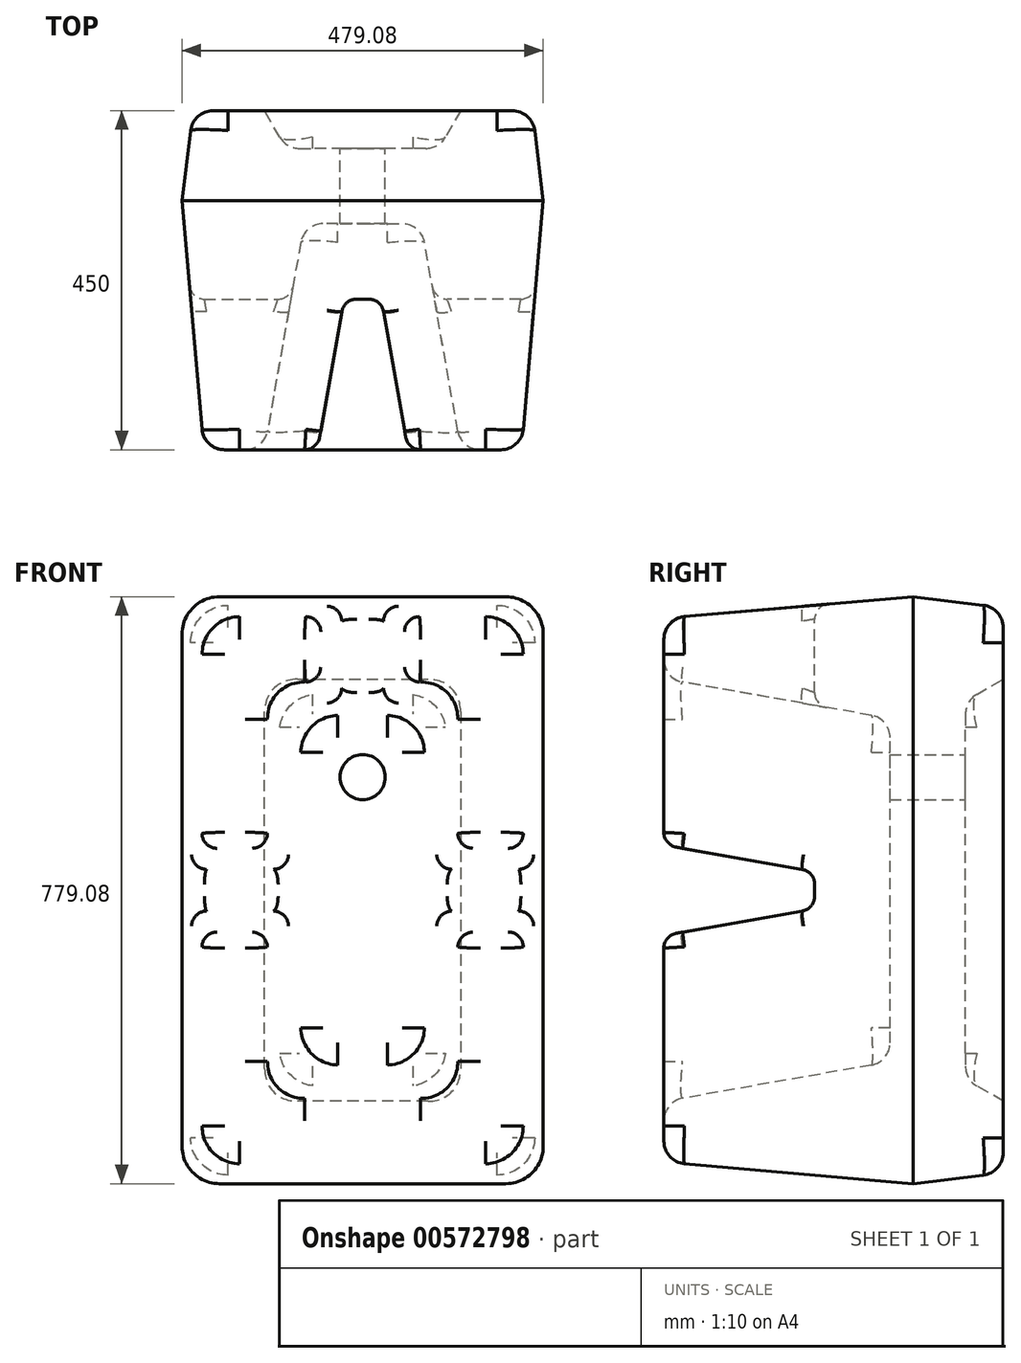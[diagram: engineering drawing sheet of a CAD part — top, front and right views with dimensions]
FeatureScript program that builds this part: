
annotation { "Feature Type Name" : "Feature", "Feature Type Description" : "" }
export const myFeature = defineFeature(function(context is Context, id is Id, definition is map)
    precondition{}
    {
        {
            var Q0;
            Q0=qCreatedBy(makeId("Front.planeOp"),FACE);
            var sketch = newSketch(context, id + "F0", { "sketchPlane" : qUnion([Q0])});
            skLineSegment(sketch, "E0.bottom", {"start": v(0, 0) * mm, "end": v(-500, 0) * mm});
            skLineSegment(sketch, "E0.top", {"start": v(0, 800) * mm, "end": v(-500, 800) * mm});
            skLineSegment(sketch, "E0.left", {"start": v(0, 0) * mm, "end": v(0, 800) * mm});
            skLineSegment(sketch, "E0.right", {"start": v(-500, 0) * mm, "end": v(-500, 800) * mm});
            skSolve(sketch);
        }
        {
            var Q0;
            Q0=makeQuery(id+"F0.imprint","IMPRINT",FACE,{"disambiguationData":[TD([[makeQuery(id+"F0.imprint","IMPRINT",EDGE,{"derivedFrom":sQuery(id+"F0.wireOp",EDGE,"E0.bottom")}),-1.0]])]});
            var sketch = newSketch(context, id + "F1", { "sketchPlane" : qUnion([Q0])});
            skSolve(sketch);
        }
        {
            var Q0;
            Q0=makeQuery(id+"F1.imprint","IMPRINT",FACE,{"disambiguationData":[TD([[makeQuery(id+"F1.imprint","IMPRINT",EDGE,{"derivedFrom":makeQuery(id+"F0.imprint","IMPRINT",EDGE,{"derivedFrom":sQuery(id+"F0.wireOp",EDGE,"E0.bottom")})}),-1.0]])]});
            extrude(context, id + "F2", {"entities" : qUnion([Q0]), "depth" : 450 * mm, "offsetDistance" : 25 * mm, "hasDraft" : true, "draftAngle" : 5 * degree, "draftPullDirection" : true});
        }
        {
            var Q0;
            Q0=makeQuery(id+"F2.opExtrude","CAP_FACE",FACE,{"disambiguationData":[OSD([sQuery(id+"F0.wireOp",EDGE,"E0.bottom"),sQuery(id+"F0.wireOp",EDGE,"E0.top"),sQuery(id+"F0.wireOp",EDGE,"E0.left"),sQuery(id+"F0.wireOp",EDGE,"E0.right")])],"isStart":false});
            var sketch = newSketch(context, id + "F3", { "sketchPlane" : qUnion([Q0])});
            skLineSegment(sketch, "E1.bottom", {"start": v(-380.63, 680.63) * mm, "end": v(-119.37, 680.63) * mm});
            skLineSegment(sketch, "E1.top", {"start": v(-380.63, 119.37) * mm, "end": v(-119.37, 119.37) * mm});
            skLineSegment(sketch, "E1.left", {"start": v(-380.63, 680.63) * mm, "end": v(-380.63, 119.37) * mm});
            skLineSegment(sketch, "E1.right", {"start": v(-119.37, 680.63) * mm, "end": v(-119.37, 119.37) * mm});
            skSolve(sketch);
        }
        {
            var Q0;
            Q0=makeQuery(id+"F3.imprint","IMPRINT",FACE,{"disambiguationData":[TD([[makeQuery(id+"F3.imprint","IMPRINT",EDGE,{"derivedFrom":sQuery(id+"F3.wireOp",EDGE,"E1.bottom")}),-1.0]])]});
            extrude(context, id + "F4", {"entities" : qUnion([Q0]), "operationType" : NewBodyOperationType.REMOVE, "oppositeDirection" : true, "depth" : 300 * mm, "offsetDistance" : 25 * mm, "hasDraft" : true, "draftAngle" : 10 * degree, "draftPullDirection" : true});
        }
        {
            var Q0;
            Q0=makeQuery(id+"F0.imprint","IMPRINT",FACE,{"disambiguationData":[TD([[makeQuery(id+"F0.imprint","IMPRINT",EDGE,{"derivedFrom":sQuery(id+"F0.wireOp",EDGE,"E0.bottom")}),-1.0]])]});
            var sketch = newSketch(context, id + "F5", { "sketchPlane" : qUnion([Q0])});
            skLineSegment(sketch, "E2.bottom", {"start": v(-380, 680) * mm, "end": v(-120, 680) * mm});
            skLineSegment(sketch, "E2.top", {"start": v(-380, 120) * mm, "end": v(-120, 120) * mm});
            skLineSegment(sketch, "E2.left", {"start": v(-380, 680) * mm, "end": v(-380, 120) * mm});
            skLineSegment(sketch, "E2.right", {"start": v(-120, 680) * mm, "end": v(-120, 120) * mm});
            skSolve(sketch);
        }
        {
            var Q0;
            Q0=makeQuery(id+"F5.imprint","IMPRINT",FACE,{"disambiguationData":[TD([[makeQuery(id+"F5.imprint","IMPRINT",EDGE,{"derivedFrom":sQuery(id+"F5.wireOp",EDGE,"E2.bottom")}),-1.0]])]});
            extrude(context, id + "F6", {"entities" : qUnion([Q0]), "operationType" : NewBodyOperationType.REMOVE, "depth" : 50 * mm, "offsetDistance" : 25 * mm, "hasDraft" : true, "draftAngle" : 30 * degree, "draftPullDirection" : true});
        }
        {
            var Q0;
            Q0=makeQuery(id+"F0.imprint","IMPRINT",FACE,{"disambiguationData":[TD([[makeQuery(id+"F0.imprint","IMPRINT",EDGE,{"derivedFrom":sQuery(id+"F0.wireOp",EDGE,"E0.bottom")}),-1.0]])]});
            var sketch = newSketch(context, id + "F7", { "sketchPlane" : qUnion([Q0])});
            skPoint(sketch, "E3", {"position": v(-250, 550) * mm});
            skSolve(sketch);
        }
        {
            var Q0;
            Q0=sQuery(id+"F7.wireOp",VERTEX,"E3");
            var Q1;
            Q1=makeQuery(id+"F2.opExtrude","SWEPT_BODY",BODY,{"disambiguationData":[OSD([sQuery(id+"F0.wireOp",EDGE,"E0.bottom"),sQuery(id+"F0.wireOp",EDGE,"E0.top"),sQuery(id+"F0.wireOp",EDGE,"E0.left"),sQuery(id+"F0.wireOp",EDGE,"E0.right")])]});
            hole(context, id + "F8", {"style" : HoleStyle.SIMPLE, "endStyle" : HoleEndStyle.THROUGH, "oppositeDirection" : true, "holeDiameter" : 60 * mm, "isTappedThrough" : true, "tappedDepth" : 12 * mm, "tapClearance" : 3, "locations" : qUnion([Q0]), "scope" : qUnion([Q1])});
        }
        {
            var Q0;
            Q0=makeQuery(id+"F2.opExtrude","CAP_EDGE",EDGE,{"disambiguationData":[OSD([sQuery(id+"F0.wireOp",EDGE,"E0.left")])],"isStart":true});
            var Q1;
            Q1=makeQuery(id+"F2.opExtrude","CAP_EDGE",EDGE,{"disambiguationData":[OSD([sQuery(id+"F0.wireOp",EDGE,"E0.bottom")])],"isStart":true});
            var Q2;
            Q2=makeQuery(id+"F2.opExtrude","CAP_EDGE",EDGE,{"disambiguationData":[OSD([sQuery(id+"F0.wireOp",EDGE,"E0.right")])],"isStart":true});
            var Q3;
            Q3=makeQuery(id+"F2.opExtrude","CAP_EDGE",EDGE,{"disambiguationData":[OSD([sQuery(id+"F0.wireOp",EDGE,"E0.top")])],"isStart":true});
            chamfer(context, id + "F9", {"entities" : qUnion([Q0, Q1, Q2, Q3]), "chamferType" : ChamferType.TWO_OFFSETS, "width1" : 120 * mm, "oppositeDirection" : false, "width2" : 25 * mm, "tangentPropagation" : true});
        }
        {
            var Q0;
            Q0=makeQuery(id+"F4.boolean.opBoolean","COPY",EDGE,{"derivedFrom":makeQuery(id+"F4.opExtrude","SWEPT_EDGE",EDGE,{"disambiguationData":[OSD([sQuery(id+"F3.wireOp",EDGE,"E1.top"),sQuery(id+"F3.wireOp",EDGE,"E1.right")])]})});
            var Q1;
            Q1=makeQuery(id+"F4.boolean.opBoolean","COPY",EDGE,{"derivedFrom":makeQuery(id+"F4.opExtrude","SWEPT_EDGE",EDGE,{"disambiguationData":[OSD([sQuery(id+"F3.wireOp",EDGE,"E1.bottom"),sQuery(id+"F3.wireOp",EDGE,"E1.right")])]})});
            var Q2;
            Q2=makeQuery(id+"F4.boolean.opBoolean","COPY",EDGE,{"derivedFrom":makeQuery(id+"F4.opExtrude","SWEPT_EDGE",EDGE,{"disambiguationData":[OSD([sQuery(id+"F3.wireOp",EDGE,"E1.bottom"),sQuery(id+"F3.wireOp",EDGE,"E1.left")])]})});
            var Q3;
            Q3=makeQuery(id+"F4.boolean.opBoolean","COPY",EDGE,{"derivedFrom":makeQuery(id+"F4.opExtrude","SWEPT_EDGE",EDGE,{"disambiguationData":[OSD([sQuery(id+"F3.wireOp",EDGE,"E1.top"),sQuery(id+"F3.wireOp",EDGE,"E1.left")])]})});
            var Q4;
            Q4=makeQuery(id+"F2.opExtrude","SWEPT_EDGE",EDGE,{"disambiguationData":[OSD([sQuery(id+"F0.wireOp",EDGE,"E0.bottom"),sQuery(id+"F0.wireOp",EDGE,"E0.left")])]});
            var Q5;
            Q5=makeQuery(id+"F2.opExtrude","SWEPT_EDGE",EDGE,{"disambiguationData":[OSD([sQuery(id+"F0.wireOp",EDGE,"E0.bottom"),sQuery(id+"F0.wireOp",EDGE,"E0.right")])]});
            var Q6;
            Q6=makeQuery(id+"F2.opExtrude","SWEPT_EDGE",EDGE,{"disambiguationData":[OSD([sQuery(id+"F0.wireOp",EDGE,"E0.top"),sQuery(id+"F0.wireOp",EDGE,"E0.left")])]});
            var Q7;
            Q7=makeQuery(id+"F9.opChamfer","BLEND_EDGE",EDGE,{"blendedFrom":[makeQuery(id+"F2.opExtrude","CAP_EDGE",EDGE,{"disambiguationData":[OSD([sQuery(id+"F0.wireOp",EDGE,"E0.bottom")])],"isStart":true}),makeQuery(id+"F2.opExtrude","CAP_EDGE",EDGE,{"disambiguationData":[OSD([sQuery(id+"F0.wireOp",EDGE,"E0.right")])],"isStart":true})],"blendedInto":[]});
            var Q8;
            Q8=makeQuery(id+"F9.opChamfer","BLEND_EDGE",EDGE,{"blendedFrom":[makeQuery(id+"F2.opExtrude","CAP_EDGE",EDGE,{"disambiguationData":[OSD([sQuery(id+"F0.wireOp",EDGE,"E0.bottom")])],"isStart":true}),makeQuery(id+"F2.opExtrude","CAP_EDGE",EDGE,{"disambiguationData":[OSD([sQuery(id+"F0.wireOp",EDGE,"E0.left")])],"isStart":true})],"blendedInto":[]});
            var Q9;
            Q9=makeQuery(id+"F9.opChamfer","BLEND_EDGE",EDGE,{"blendedFrom":[makeQuery(id+"F2.opExtrude","CAP_EDGE",EDGE,{"disambiguationData":[OSD([sQuery(id+"F0.wireOp",EDGE,"E0.top")])],"isStart":true}),makeQuery(id+"F2.opExtrude","CAP_EDGE",EDGE,{"disambiguationData":[OSD([sQuery(id+"F0.wireOp",EDGE,"E0.left")])],"isStart":true})],"blendedInto":[]});
            var Q10;
            Q10=makeQuery(id+"F2.opExtrude","SWEPT_EDGE",EDGE,{"disambiguationData":[OSD([sQuery(id+"F0.wireOp",EDGE,"E0.top"),sQuery(id+"F0.wireOp",EDGE,"E0.right")])]});
            var Q11;
            Q11=makeQuery(id+"F9.opChamfer","BLEND_EDGE",EDGE,{"blendedFrom":[makeQuery(id+"F2.opExtrude","CAP_EDGE",EDGE,{"disambiguationData":[OSD([sQuery(id+"F0.wireOp",EDGE,"E0.top")])],"isStart":true}),makeQuery(id+"F2.opExtrude","CAP_EDGE",EDGE,{"disambiguationData":[OSD([sQuery(id+"F0.wireOp",EDGE,"E0.right")])],"isStart":true})],"blendedInto":[]});
            var Q12;
            Q12=makeQuery(id+"F6.boolean.opBoolean","COPY",EDGE,{"derivedFrom":makeQuery(id+"F6.opExtrude","SWEPT_EDGE",EDGE,{"disambiguationData":[OSD([sQuery(id+"F5.wireOp",EDGE,"E2.bottom"),sQuery(id+"F5.wireOp",EDGE,"E2.right")])]})});
            var Q13;
            Q13=makeQuery(id+"F6.boolean.opBoolean","COPY",EDGE,{"derivedFrom":makeQuery(id+"F6.opExtrude","SWEPT_EDGE",EDGE,{"disambiguationData":[OSD([sQuery(id+"F5.wireOp",EDGE,"E2.bottom"),sQuery(id+"F5.wireOp",EDGE,"E2.left")])]})});
            var Q14;
            Q14=makeQuery(id+"F6.boolean.opBoolean","COPY",EDGE,{"derivedFrom":makeQuery(id+"F6.opExtrude","SWEPT_EDGE",EDGE,{"disambiguationData":[OSD([sQuery(id+"F5.wireOp",EDGE,"E2.top"),sQuery(id+"F5.wireOp",EDGE,"E2.left")])]})});
            var Q15;
            Q15=makeQuery(id+"F6.boolean.opBoolean","COPY",EDGE,{"derivedFrom":makeQuery(id+"F6.opExtrude","SWEPT_EDGE",EDGE,{"disambiguationData":[OSD([sQuery(id+"F5.wireOp",EDGE,"E2.top"),sQuery(id+"F5.wireOp",EDGE,"E2.right")])]})});
            fillet(context, id + "F10", {"entities" : qUnion([Q0, Q1, Q2, Q3, Q4, Q5, Q6, Q7, Q8, Q9, Q10, Q11, Q12, Q13, Q14, Q15]), "radius" : 50 * mm, "tangentPropagation" : true, "defaultsChanged" : true, "vertexSettings" : [], "allowEdgeOverflow" : false});
        }
        {
            var Q0;
            {var subQ0=sQuery(id+"F3.wireOp",EDGE,"E1.right");var subQ1=sQuery(id+"F3.wireOp",EDGE,"E1.bottom");Q0=makeQuery(id+"F10.opFillet","BLEND_EDGE",EDGE,{"blendedFrom":[makeQuery(id+"F4.boolean.opBoolean","COPY",EDGE,{"derivedFrom":makeQuery(id+"F4.opExtrude","SWEPT_EDGE",EDGE,{"disambiguationData":[OSD([subQ1,subQ0])]})}),makeQuery(id+"F4.boolean.opBoolean","COPY",FACE,{"derivedFrom":makeQuery(id+"F4.opExtrude","CAP_FACE",FACE,{"disambiguationData":[OSD([subQ1,sQuery(id+"F3.wireOp",EDGE,"E1.top"),sQuery(id+"F3.wireOp",EDGE,"E1.left"),subQ0])],"isStart":false})})],"blendedInto":[makeQuery(id+"F4.boolean.opBoolean","COPY",FACE,{"derivedFrom":makeQuery(id+"F4.opExtrude","CAP_FACE",FACE,{"disambiguationData":[OSD([subQ1,sQuery(id+"F3.wireOp",EDGE,"E1.top"),sQuery(id+"F3.wireOp",EDGE,"E1.left"),subQ0])],"isStart":false})})]});}
            var Q1;
            Q1=makeQuery(id+"F10.opFillet","BLEND_EDGE",EDGE,{"blendedFrom":[makeQuery(id+"F4.boolean.opBoolean","COPY",EDGE,{"derivedFrom":makeQuery(id+"F4.opExtrude","SWEPT_EDGE",EDGE,{"disambiguationData":[OSD([sQuery(id+"F3.wireOp",EDGE,"E1.bottom"),sQuery(id+"F3.wireOp",EDGE,"E1.right")])]})}),makeQuery(id+"F2.opExtrude","CAP_FACE",FACE,{"disambiguationData":[OSD([sQuery(id+"F0.wireOp",EDGE,"E0.bottom"),sQuery(id+"F0.wireOp",EDGE,"E0.top"),sQuery(id+"F0.wireOp",EDGE,"E0.left"),sQuery(id+"F0.wireOp",EDGE,"E0.right")])],"isStart":false})],"blendedInto":[makeQuery(id+"F2.opExtrude","CAP_FACE",FACE,{"disambiguationData":[OSD([sQuery(id+"F0.wireOp",EDGE,"E0.bottom"),sQuery(id+"F0.wireOp",EDGE,"E0.top"),sQuery(id+"F0.wireOp",EDGE,"E0.left"),sQuery(id+"F0.wireOp",EDGE,"E0.right")])],"isStart":false})]});
            var Q2;
            {var subQ0=sQuery(id+"F0.wireOp",EDGE,"E0.left");var subQ1=sQuery(id+"F0.wireOp",EDGE,"E0.top");Q2=makeQuery(id+"F10.opFillet","BLEND_EDGE",EDGE,{"blendedFrom":[makeQuery(id+"F2.opExtrude","SWEPT_EDGE",EDGE,{"disambiguationData":[OSD([subQ1,subQ0])]}),makeQuery(id+"F2.opExtrude","CAP_FACE",FACE,{"disambiguationData":[OSD([sQuery(id+"F0.wireOp",EDGE,"E0.bottom"),subQ1,subQ0,sQuery(id+"F0.wireOp",EDGE,"E0.right")])],"isStart":false})],"blendedInto":[makeQuery(id+"F2.opExtrude","CAP_FACE",FACE,{"disambiguationData":[OSD([sQuery(id+"F0.wireOp",EDGE,"E0.bottom"),subQ1,subQ0,sQuery(id+"F0.wireOp",EDGE,"E0.right")])],"isStart":false})]});}
            var Q3;
            {var subQ0=sQuery(id+"F0.wireOp",EDGE,"E0.left");Q3=makeQuery(id+"F9.opChamfer","BLEND_EDGE",EDGE,{"blendedFrom":[makeQuery(id+"F2.opExtrude","CAP_EDGE",EDGE,{"disambiguationData":[OSD([subQ0])],"isStart":true}),makeQuery(id+"F2.opExtrude","CAP_FACE",FACE,{"disambiguationData":[OSD([sQuery(id+"F0.wireOp",EDGE,"E0.bottom"),sQuery(id+"F0.wireOp",EDGE,"E0.top"),subQ0,sQuery(id+"F0.wireOp",EDGE,"E0.right")])],"isStart":true})],"blendedInto":[makeQuery(id+"F2.opExtrude","CAP_FACE",FACE,{"disambiguationData":[OSD([sQuery(id+"F0.wireOp",EDGE,"E0.bottom"),sQuery(id+"F0.wireOp",EDGE,"E0.top"),subQ0,sQuery(id+"F0.wireOp",EDGE,"E0.right")])],"isStart":true})]});}
            var Q4;
            Q4=makeQuery(id+"F6.boolean.opBoolean","COPY",EDGE,{"derivedFrom":makeQuery(id+"F6.opExtrude","CAP_EDGE",EDGE,{"disambiguationData":[OSD([sQuery(id+"F5.wireOp",EDGE,"E2.top")])],"isStart":true})});
            var Q5;
            Q5=makeQuery(id+"F6.boolean.opBoolean","COPY",EDGE,{"derivedFrom":makeQuery(id+"F6.opExtrude","CAP_EDGE",EDGE,{"disambiguationData":[OSD([sQuery(id+"F5.wireOp",EDGE,"E2.top")])],"isStart":false})});
            fillet(context, id + "F11", {"entities" : qUnion([Q0, Q1, Q2, Q3, Q4, Q5]), "radius" : 30 * mm, "tangentPropagation" : true, "allowEdgeOverflow" : false});
        }
        {
            var Q0;
            Q0=makeQuery(id+"F2.opExtrude","CAP_FACE",FACE,{"disambiguationData":[OSD([sQuery(id+"F0.wireOp",EDGE,"E0.bottom"),sQuery(id+"F0.wireOp",EDGE,"E0.top"),sQuery(id+"F0.wireOp",EDGE,"E0.left"),sQuery(id+"F0.wireOp",EDGE,"E0.right")])],"isStart":false});
            var sketch = newSketch(context, id + "F12", { "sketchPlane" : qUnion([Q0])});
            skLineSegment(sketch, "E4.bottom", {"start": v(-190, 257.75) * mm, "end": v(-310, 257.75) * mm});
            skLineSegment(sketch, "E4.top", {"start": v(-190, 1153.86) * mm, "end": v(-310, 1153.86) * mm});
            skLineSegment(sketch, "E4.left", {"start": v(-190, 257.75) * mm, "end": v(-190, 1153.86) * mm});
            skLineSegment(sketch, "E4.right", {"start": v(-310, 257.75) * mm, "end": v(-310, 1153.86) * mm});
            skPoint(sketch, "E4.middle", {"position": v(-250, 705.8) * mm});
            skLineSegment(sketch, "E5.bottom", {"start": v(130.25, 340) * mm, "end": v(-941.86, 340) * mm});
            skLineSegment(sketch, "E5.top", {"start": v(130.25, 460) * mm, "end": v(-941.86, 460) * mm});
            skLineSegment(sketch, "E5.left", {"start": v(130.25, 340) * mm, "end": v(130.25, 460) * mm});
            skLineSegment(sketch, "E5.right", {"start": v(-941.86, 340) * mm, "end": v(-941.86, 460) * mm});
            skPoint(sketch, "E5.middle", {"position": v(-405.8, 400) * mm});
            skSolve(sketch);
        }
        {
            var Q0;
            {var subQ0=sQuery(id+"F12.wireOp",EDGE,"E5.bottom");var subQ1=sQuery(id+"F12.wireOp",EDGE,"E4.right");var subQ2=makeQuery(id+"F12.imprint","INTERSECT",VERTEX,{"derivedFrom":[subQ1,subQ0]});Q0=makeQuery(id+"F12.imprint","IMPRINT",FACE,{"disambiguationData":[TD([[makeQuery(id+"F12.imprint","IMPRINT",EDGE,{"disambiguationData":[TD([[subQ2,-1.0]])],"derivedFrom":subQ1}),1.0]])]});}
            var Q1;
            {var subQ0=sQuery(id+"F12.wireOp",EDGE,"E5.bottom");var subQ1=sQuery(id+"F0.wireOp",EDGE,"E0.right");var subQ2=makeQuery(id+"F2.opExtrude","CAP_FACE",FACE,{"disambiguationData":[OSD([sQuery(id+"F0.wireOp",EDGE,"E0.bottom"),sQuery(id+"F0.wireOp",EDGE,"E0.top"),sQuery(id+"F0.wireOp",EDGE,"E0.left"),subQ1])],"isStart":false});var subQ3=makeQuery(id+"F11.opFillet","BLEND_EDGE",EDGE,{"blendedFrom":[makeQuery(id+"F2.opExtrude","CAP_EDGE",EDGE,{"disambiguationData":[OSD([subQ1])],"isStart":false}),subQ2],"blendedInto":[subQ2]});var subQ4=makeQuery(id+"F12.imprint","INTERSECT",VERTEX,{"derivedFrom":[subQ3,subQ0]});Q1=makeQuery(id+"F12.imprint","IMPRINT",FACE,{"disambiguationData":[TD([[makeQuery(id+"F12.imprint","IMPRINT",EDGE,{"disambiguationData":[TD([[subQ4,1.0]])],"derivedFrom":subQ0}),-1.0]])]});}
            var Q2;
            {var subQ0=sQuery(id+"F12.wireOp",EDGE,"E5.right");Q2=makeQuery(id+"F12.imprint","IMPRINT",FACE,{"disambiguationData":[TD([[makeQuery(id+"F12.imprint","IMPRINT",EDGE,{"derivedFrom":subQ0}),-1.0]])]});}
            var Q3;
            {var subQ0=sQuery(id+"F12.wireOp",EDGE,"E5.bottom");var subQ1=sQuery(id+"F12.wireOp",EDGE,"E4.left");var subQ2=makeQuery(id+"F12.imprint","INTERSECT",VERTEX,{"derivedFrom":[subQ1,subQ0]});Q3=makeQuery(id+"F12.imprint","IMPRINT",FACE,{"disambiguationData":[TD([[makeQuery(id+"F12.imprint","IMPRINT",EDGE,{"disambiguationData":[TD([[subQ2,-1.0]])],"derivedFrom":subQ1}),1.0]])]});}
            var Q4;
            {var subQ0=sQuery(id+"F12.wireOp",EDGE,"E5.top");var subQ1=sQuery(id+"F12.wireOp",EDGE,"E4.left");var subQ2=makeQuery(id+"F12.imprint","INTERSECT",VERTEX,{"derivedFrom":[subQ1,subQ0]});Q4=makeQuery(id+"F12.imprint","IMPRINT",FACE,{"disambiguationData":[TD([[makeQuery(id+"F12.imprint","IMPRINT",EDGE,{"disambiguationData":[TD([[subQ2,-1.0]])],"derivedFrom":subQ0}),-1.0]])]});}
            var Q5;
            {var subQ0=sQuery(id+"F12.wireOp",EDGE,"E5.bottom");var subQ1=sQuery(id+"F12.wireOp",EDGE,"E4.left");var subQ2=makeQuery(id+"F12.imprint","INTERSECT",VERTEX,{"derivedFrom":[subQ1,subQ0]});Q5=makeQuery(id+"F12.imprint","IMPRINT",FACE,{"disambiguationData":[TD([[makeQuery(id+"F12.imprint","IMPRINT",EDGE,{"disambiguationData":[TD([[subQ2,-1.0]])],"derivedFrom":subQ0}),1.0]])]});}
            var Q6;
            {var subQ0=sQuery(id+"F12.wireOp",EDGE,"E5.bottom");var subQ1=sQuery(id+"F12.wireOp",EDGE,"E4.left");var subQ2=makeQuery(id+"F12.imprint","INTERSECT",VERTEX,{"derivedFrom":[subQ1,subQ0]});Q6=makeQuery(id+"F12.imprint","IMPRINT",FACE,{"disambiguationData":[TD([[makeQuery(id+"F12.imprint","IMPRINT",EDGE,{"disambiguationData":[TD([[subQ2,-1.0]])],"derivedFrom":subQ1}),-1.0]])]});}
            var Q7;
            {var subQ0=sQuery(id+"F12.wireOp",EDGE,"E5.bottom");var subQ1=sQuery(id+"F0.wireOp",EDGE,"E0.left");var subQ2=makeQuery(id+"F2.opExtrude","CAP_FACE",FACE,{"disambiguationData":[OSD([sQuery(id+"F0.wireOp",EDGE,"E0.bottom"),sQuery(id+"F0.wireOp",EDGE,"E0.top"),subQ1,sQuery(id+"F0.wireOp",EDGE,"E0.right")])],"isStart":false});var subQ3=makeQuery(id+"F11.opFillet","BLEND_EDGE",EDGE,{"blendedFrom":[makeQuery(id+"F2.opExtrude","CAP_EDGE",EDGE,{"disambiguationData":[OSD([subQ1])],"isStart":false}),subQ2],"blendedInto":[subQ2]});var subQ4=makeQuery(id+"F12.imprint","INTERSECT",VERTEX,{"derivedFrom":[subQ3,subQ0]});Q7=makeQuery(id+"F12.imprint","IMPRINT",FACE,{"disambiguationData":[TD([[makeQuery(id+"F12.imprint","IMPRINT",EDGE,{"disambiguationData":[TD([[subQ4,-1.0]])],"derivedFrom":subQ0}),-1.0]])]});}
            var Q8;
            {var subQ0=sQuery(id+"F12.wireOp",EDGE,"E5.left");Q8=makeQuery(id+"F12.imprint","IMPRINT",FACE,{"disambiguationData":[TD([[makeQuery(id+"F12.imprint","IMPRINT",EDGE,{"derivedFrom":subQ0}),1.0]])]});}
            var Q9;
            {var subQ0=sQuery(id+"F12.wireOp",EDGE,"E4.bottom");Q9=makeQuery(id+"F12.imprint","IMPRINT",FACE,{"disambiguationData":[TD([[makeQuery(id+"F12.imprint","IMPRINT",EDGE,{"derivedFrom":subQ0}),-1.0]])]});}
            var Q10;
            {var subQ0=sQuery(id+"F12.wireOp",EDGE,"E4.left");var subQ1=sQuery(id+"F0.wireOp",EDGE,"E0.bottom");var subQ2=makeQuery(id+"F2.opExtrude","CAP_FACE",FACE,{"disambiguationData":[OSD([subQ1,sQuery(id+"F0.wireOp",EDGE,"E0.top"),sQuery(id+"F0.wireOp",EDGE,"E0.left"),sQuery(id+"F0.wireOp",EDGE,"E0.right")])],"isStart":false});var subQ3=makeQuery(id+"F11.opFillet","BLEND_EDGE",EDGE,{"blendedFrom":[makeQuery(id+"F2.opExtrude","CAP_EDGE",EDGE,{"disambiguationData":[OSD([subQ1])],"isStart":false}),subQ2],"blendedInto":[subQ2]});var subQ4=makeQuery(id+"F12.imprint","INTERSECT",VERTEX,{"derivedFrom":[subQ3,subQ0]});Q10=makeQuery(id+"F12.imprint","IMPRINT",FACE,{"disambiguationData":[TD([[makeQuery(id+"F12.imprint","IMPRINT",EDGE,{"disambiguationData":[TD([[subQ4,-1.0]])],"derivedFrom":subQ0}),1.0]])]});}
            var Q11;
            {var subQ0=sQuery(id+"F12.wireOp",EDGE,"E4.left");var subQ1=sQuery(id+"F0.wireOp",EDGE,"E0.top");var subQ2=makeQuery(id+"F2.opExtrude","CAP_FACE",FACE,{"disambiguationData":[OSD([sQuery(id+"F0.wireOp",EDGE,"E0.bottom"),subQ1,sQuery(id+"F0.wireOp",EDGE,"E0.left"),sQuery(id+"F0.wireOp",EDGE,"E0.right")])],"isStart":false});var subQ3=makeQuery(id+"F11.opFillet","BLEND_EDGE",EDGE,{"blendedFrom":[makeQuery(id+"F2.opExtrude","CAP_EDGE",EDGE,{"disambiguationData":[OSD([subQ1])],"isStart":false}),subQ2],"blendedInto":[subQ2]});var subQ4=makeQuery(id+"F12.imprint","INTERSECT",VERTEX,{"derivedFrom":[subQ3,subQ0]});Q11=makeQuery(id+"F12.imprint","IMPRINT",FACE,{"disambiguationData":[TD([[makeQuery(id+"F12.imprint","IMPRINT",EDGE,{"disambiguationData":[TD([[subQ4,1.0]])],"derivedFrom":subQ0}),1.0]])]});}
            var Q12;
            {var subQ0=sQuery(id+"F12.wireOp",EDGE,"E4.top");Q12=makeQuery(id+"F12.imprint","IMPRINT",FACE,{"disambiguationData":[TD([[makeQuery(id+"F12.imprint","IMPRINT",EDGE,{"derivedFrom":subQ0}),1.0]])]});}
            extrude(context, id + "F13", {"entities" : qUnion([Q0, Q1, Q2, Q3, Q4, Q5, Q6, Q7, Q8, Q9, Q10, Q11, Q12]), "operationType" : NewBodyOperationType.REMOVE, "oppositeDirection" : true, "depth" : 200 * mm, "offsetDistance" : 25 * mm, "hasDraft" : true, "draftAngle" : 10 * degree, "draftPullDirection" : true});
        }
        {
            var Q0;
            {var subQ0=sQuery(id+"F12.wireOp",EDGE,"E5.top");var subQ1=sQuery(id+"F0.wireOp",EDGE,"E0.right");var subQ2=makeQuery(id+"F2.opExtrude","CAP_FACE",FACE,{"disambiguationData":[OSD([sQuery(id+"F0.wireOp",EDGE,"E0.bottom"),sQuery(id+"F0.wireOp",EDGE,"E0.top"),sQuery(id+"F0.wireOp",EDGE,"E0.left"),subQ1])],"isStart":false});var subQ3=makeQuery(id+"F12.imprint","INTERSECT",VERTEX,{"derivedFrom":[makeQuery(id+"F11.opFillet","BLEND_EDGE",EDGE,{"blendedFrom":[makeQuery(id+"F2.opExtrude","CAP_EDGE",EDGE,{"disambiguationData":[OSD([subQ1])],"isStart":false}),subQ2],"blendedInto":[subQ2]}),subQ0]});Q0=makeQuery(id+"F13.boolean.opBoolean","COPY",EDGE,{"derivedFrom":makeQuery(id+"F13.opExtrude","CAP_EDGE",EDGE,{"disambiguationData":[OSD([subQ0]),TDD([makeQuery(id+"F12.imprint","IMPRINT",EDGE,{"disambiguationData":[TD([[makeQuery(id+"F12.imprint","INTERSECT",VERTEX,{"derivedFrom":[sQuery(id+"F12.wireOp",EDGE,"E4.right"),subQ0]}),-1.0]])],"derivedFrom":subQ0}),makeQuery(id+"F12.imprint","IMPRINT",EDGE,{"disambiguationData":[TD([[subQ3,1.0]])],"derivedFrom":subQ0}),makeQuery(id+"F12.imprint","IMPRINT",EDGE,{"disambiguationData":[TD([[makeQuery(id+"F12.imprint","INTERSECT",VERTEX,{"derivedFrom":[subQ0,sQuery(id+"F12.wireOp",EDGE,"E5.right")]}),1.0]])],"derivedFrom":subQ0})])],"isStart":false})});}
            var Q1;
            {var subQ0=sQuery(id+"F12.wireOp",EDGE,"E5.bottom");var subQ1=sQuery(id+"F0.wireOp",EDGE,"E0.right");var subQ2=makeQuery(id+"F2.opExtrude","CAP_FACE",FACE,{"disambiguationData":[OSD([sQuery(id+"F0.wireOp",EDGE,"E0.bottom"),sQuery(id+"F0.wireOp",EDGE,"E0.top"),sQuery(id+"F0.wireOp",EDGE,"E0.left"),subQ1])],"isStart":false});var subQ3=makeQuery(id+"F12.imprint","INTERSECT",VERTEX,{"derivedFrom":[makeQuery(id+"F11.opFillet","BLEND_EDGE",EDGE,{"blendedFrom":[makeQuery(id+"F2.opExtrude","CAP_EDGE",EDGE,{"disambiguationData":[OSD([subQ1])],"isStart":false}),subQ2],"blendedInto":[subQ2]}),subQ0]});Q1=makeQuery(id+"F13.boolean.opBoolean","COPY",EDGE,{"derivedFrom":makeQuery(id+"F13.opExtrude","CAP_EDGE",EDGE,{"disambiguationData":[OSD([subQ0]),TDD([makeQuery(id+"F12.imprint","IMPRINT",EDGE,{"disambiguationData":[TD([[makeQuery(id+"F12.imprint","INTERSECT",VERTEX,{"derivedFrom":[sQuery(id+"F12.wireOp",EDGE,"E4.right"),subQ0]}),-1.0]])],"derivedFrom":subQ0}),makeQuery(id+"F12.imprint","IMPRINT",EDGE,{"disambiguationData":[TD([[subQ3,1.0]])],"derivedFrom":subQ0}),makeQuery(id+"F12.imprint","IMPRINT",EDGE,{"disambiguationData":[TD([[makeQuery(id+"F12.imprint","INTERSECT",VERTEX,{"derivedFrom":[subQ0,sQuery(id+"F12.wireOp",EDGE,"E5.right")]}),1.0]])],"derivedFrom":subQ0})])],"isStart":false})});}
            var Q2;
            {var subQ0=sQuery(id+"F12.wireOp",EDGE,"E4.right");var subQ1=sQuery(id+"F0.wireOp",EDGE,"E0.top");var subQ2=makeQuery(id+"F2.opExtrude","CAP_FACE",FACE,{"disambiguationData":[OSD([sQuery(id+"F0.wireOp",EDGE,"E0.bottom"),subQ1,sQuery(id+"F0.wireOp",EDGE,"E0.left"),sQuery(id+"F0.wireOp",EDGE,"E0.right")])],"isStart":false});var subQ3=makeQuery(id+"F12.imprint","INTERSECT",VERTEX,{"derivedFrom":[makeQuery(id+"F11.opFillet","BLEND_EDGE",EDGE,{"blendedFrom":[makeQuery(id+"F2.opExtrude","CAP_EDGE",EDGE,{"disambiguationData":[OSD([subQ1])],"isStart":false}),subQ2],"blendedInto":[subQ2]}),subQ0]});Q2=makeQuery(id+"F13.boolean.opBoolean","COPY",EDGE,{"derivedFrom":makeQuery(id+"F13.opExtrude","CAP_EDGE",EDGE,{"disambiguationData":[OSD([subQ0]),TDD([makeQuery(id+"F12.imprint","IMPRINT",EDGE,{"disambiguationData":[TD([[makeQuery(id+"F12.imprint","INTERSECT",VERTEX,{"derivedFrom":[subQ0,sQuery(id+"F12.wireOp",EDGE,"E5.top")]}),-1.0]])],"derivedFrom":subQ0}),makeQuery(id+"F12.imprint","IMPRINT",EDGE,{"disambiguationData":[TD([[subQ3,1.0]])],"derivedFrom":subQ0}),makeQuery(id+"F12.imprint","IMPRINT",EDGE,{"disambiguationData":[TD([[makeQuery(id+"F12.imprint","INTERSECT",VERTEX,{"derivedFrom":[sQuery(id+"F12.wireOp",EDGE,"E4.top"),subQ0]}),1.0]])],"derivedFrom":subQ0})])],"isStart":false})});}
            var Q3;
            {var subQ0=sQuery(id+"F12.wireOp",EDGE,"E4.left");var subQ1=sQuery(id+"F0.wireOp",EDGE,"E0.top");var subQ2=makeQuery(id+"F2.opExtrude","CAP_FACE",FACE,{"disambiguationData":[OSD([sQuery(id+"F0.wireOp",EDGE,"E0.bottom"),subQ1,sQuery(id+"F0.wireOp",EDGE,"E0.left"),sQuery(id+"F0.wireOp",EDGE,"E0.right")])],"isStart":false});var subQ3=makeQuery(id+"F12.imprint","INTERSECT",VERTEX,{"derivedFrom":[makeQuery(id+"F11.opFillet","BLEND_EDGE",EDGE,{"blendedFrom":[makeQuery(id+"F2.opExtrude","CAP_EDGE",EDGE,{"disambiguationData":[OSD([subQ1])],"isStart":false}),subQ2],"blendedInto":[subQ2]}),subQ0]});Q3=makeQuery(id+"F13.boolean.opBoolean","COPY",EDGE,{"derivedFrom":makeQuery(id+"F13.opExtrude","CAP_EDGE",EDGE,{"disambiguationData":[OSD([subQ0]),TDD([makeQuery(id+"F12.imprint","IMPRINT",EDGE,{"disambiguationData":[TD([[makeQuery(id+"F12.imprint","INTERSECT",VERTEX,{"derivedFrom":[subQ0,sQuery(id+"F12.wireOp",EDGE,"E5.top")]}),-1.0]])],"derivedFrom":subQ0}),makeQuery(id+"F12.imprint","IMPRINT",EDGE,{"disambiguationData":[TD([[subQ3,1.0]])],"derivedFrom":subQ0}),makeQuery(id+"F12.imprint","IMPRINT",EDGE,{"disambiguationData":[TD([[makeQuery(id+"F12.imprint","INTERSECT",VERTEX,{"derivedFrom":[sQuery(id+"F12.wireOp",EDGE,"E4.top"),subQ0]}),1.0]])],"derivedFrom":subQ0})])],"isStart":false})});}
            var Q4;
            {var subQ0=sQuery(id+"F12.wireOp",EDGE,"E5.bottom");var subQ1=sQuery(id+"F0.wireOp",EDGE,"E0.left");var subQ2=makeQuery(id+"F2.opExtrude","CAP_FACE",FACE,{"disambiguationData":[OSD([sQuery(id+"F0.wireOp",EDGE,"E0.bottom"),sQuery(id+"F0.wireOp",EDGE,"E0.top"),subQ1,sQuery(id+"F0.wireOp",EDGE,"E0.right")])],"isStart":false});var subQ4=makeQuery(id+"F12.imprint","INTERSECT",VERTEX,{"derivedFrom":[makeQuery(id+"F11.opFillet","BLEND_EDGE",EDGE,{"blendedFrom":[makeQuery(id+"F2.opExtrude","CAP_EDGE",EDGE,{"disambiguationData":[OSD([subQ1])],"isStart":false}),subQ2],"blendedInto":[subQ2]}),subQ0]});Q4=makeQuery(id+"F13.boolean.opBoolean","COPY",EDGE,{"derivedFrom":makeQuery(id+"F13.opExtrude","CAP_EDGE",EDGE,{"disambiguationData":[OSD([subQ0]),TDD([makeQuery(id+"F12.imprint","IMPRINT",EDGE,{"disambiguationData":[TD([[makeQuery(id+"F12.imprint","INTERSECT",VERTEX,{"derivedFrom":[subQ0,sQuery(id+"F12.wireOp",EDGE,"E5.left")]}),-1.0]])],"derivedFrom":subQ0}),makeQuery(id+"F12.imprint","IMPRINT",EDGE,{"disambiguationData":[TD([[subQ4,-1.0]])],"derivedFrom":subQ0}),makeQuery(id+"F12.imprint","IMPRINT",EDGE,{"disambiguationData":[TD([[makeQuery(id+"F12.imprint","INTERSECT",VERTEX,{"derivedFrom":[sQuery(id+"F12.wireOp",EDGE,"E4.left"),subQ0]}),1.0]])],"derivedFrom":subQ0})])],"isStart":false})});}
            var Q5;
            {var subQ0=sQuery(id+"F12.wireOp",EDGE,"E5.top");var subQ1=sQuery(id+"F0.wireOp",EDGE,"E0.left");var subQ2=makeQuery(id+"F2.opExtrude","CAP_FACE",FACE,{"disambiguationData":[OSD([sQuery(id+"F0.wireOp",EDGE,"E0.bottom"),sQuery(id+"F0.wireOp",EDGE,"E0.top"),subQ1,sQuery(id+"F0.wireOp",EDGE,"E0.right")])],"isStart":false});var subQ4=makeQuery(id+"F12.imprint","INTERSECT",VERTEX,{"derivedFrom":[makeQuery(id+"F11.opFillet","BLEND_EDGE",EDGE,{"blendedFrom":[makeQuery(id+"F2.opExtrude","CAP_EDGE",EDGE,{"disambiguationData":[OSD([subQ1])],"isStart":false}),subQ2],"blendedInto":[subQ2]}),subQ0]});Q5=makeQuery(id+"F13.boolean.opBoolean","COPY",EDGE,{"derivedFrom":makeQuery(id+"F13.opExtrude","CAP_EDGE",EDGE,{"disambiguationData":[OSD([subQ0]),TDD([makeQuery(id+"F12.imprint","IMPRINT",EDGE,{"disambiguationData":[TD([[makeQuery(id+"F12.imprint","INTERSECT",VERTEX,{"derivedFrom":[subQ0,sQuery(id+"F12.wireOp",EDGE,"E5.left")]}),-1.0]])],"derivedFrom":subQ0}),makeQuery(id+"F12.imprint","IMPRINT",EDGE,{"disambiguationData":[TD([[subQ4,-1.0]])],"derivedFrom":subQ0}),makeQuery(id+"F12.imprint","IMPRINT",EDGE,{"disambiguationData":[TD([[makeQuery(id+"F12.imprint","INTERSECT",VERTEX,{"derivedFrom":[sQuery(id+"F12.wireOp",EDGE,"E4.left"),subQ0]}),1.0]])],"derivedFrom":subQ0})])],"isStart":false})});}
            var Q6;
            {var subQ0=sQuery(id+"F12.wireOp",EDGE,"E4.right");var subQ1=sQuery(id+"F0.wireOp",EDGE,"E0.bottom");var subQ2=makeQuery(id+"F2.opExtrude","CAP_FACE",FACE,{"disambiguationData":[OSD([subQ1,sQuery(id+"F0.wireOp",EDGE,"E0.top"),sQuery(id+"F0.wireOp",EDGE,"E0.left"),sQuery(id+"F0.wireOp",EDGE,"E0.right")])],"isStart":false});var subQ4=makeQuery(id+"F12.imprint","INTERSECT",VERTEX,{"derivedFrom":[makeQuery(id+"F11.opFillet","BLEND_EDGE",EDGE,{"blendedFrom":[makeQuery(id+"F2.opExtrude","CAP_EDGE",EDGE,{"disambiguationData":[OSD([subQ1])],"isStart":false}),subQ2],"blendedInto":[subQ2]}),subQ0]});Q6=makeQuery(id+"F13.boolean.opBoolean","COPY",EDGE,{"derivedFrom":makeQuery(id+"F13.opExtrude","CAP_EDGE",EDGE,{"disambiguationData":[OSD([subQ0]),TDD([makeQuery(id+"F12.imprint","IMPRINT",EDGE,{"disambiguationData":[TD([[makeQuery(id+"F12.imprint","INTERSECT",VERTEX,{"derivedFrom":[sQuery(id+"F12.wireOp",EDGE,"E4.bottom"),subQ0]}),-1.0]])],"derivedFrom":subQ0}),makeQuery(id+"F12.imprint","IMPRINT",EDGE,{"disambiguationData":[TD([[subQ4,-1.0]])],"derivedFrom":subQ0}),makeQuery(id+"F12.imprint","IMPRINT",EDGE,{"disambiguationData":[TD([[makeQuery(id+"F12.imprint","INTERSECT",VERTEX,{"derivedFrom":[subQ0,sQuery(id+"F12.wireOp",EDGE,"E5.bottom")]}),1.0]])],"derivedFrom":subQ0})])],"isStart":false})});}
            var Q7;
            {var subQ0=sQuery(id+"F12.wireOp",EDGE,"E4.left");var subQ1=sQuery(id+"F0.wireOp",EDGE,"E0.bottom");var subQ2=makeQuery(id+"F2.opExtrude","CAP_FACE",FACE,{"disambiguationData":[OSD([subQ1,sQuery(id+"F0.wireOp",EDGE,"E0.top"),sQuery(id+"F0.wireOp",EDGE,"E0.left"),sQuery(id+"F0.wireOp",EDGE,"E0.right")])],"isStart":false});var subQ4=makeQuery(id+"F12.imprint","INTERSECT",VERTEX,{"derivedFrom":[makeQuery(id+"F11.opFillet","BLEND_EDGE",EDGE,{"blendedFrom":[makeQuery(id+"F2.opExtrude","CAP_EDGE",EDGE,{"disambiguationData":[OSD([subQ1])],"isStart":false}),subQ2],"blendedInto":[subQ2]}),subQ0]});Q7=makeQuery(id+"F13.boolean.opBoolean","COPY",EDGE,{"derivedFrom":makeQuery(id+"F13.opExtrude","CAP_EDGE",EDGE,{"disambiguationData":[OSD([subQ0]),TDD([makeQuery(id+"F12.imprint","IMPRINT",EDGE,{"disambiguationData":[TD([[makeQuery(id+"F12.imprint","INTERSECT",VERTEX,{"derivedFrom":[sQuery(id+"F12.wireOp",EDGE,"E4.bottom"),subQ0]}),-1.0]])],"derivedFrom":subQ0}),makeQuery(id+"F12.imprint","IMPRINT",EDGE,{"disambiguationData":[TD([[subQ4,-1.0]])],"derivedFrom":subQ0}),makeQuery(id+"F12.imprint","IMPRINT",EDGE,{"disambiguationData":[TD([[makeQuery(id+"F12.imprint","INTERSECT",VERTEX,{"derivedFrom":[subQ0,sQuery(id+"F12.wireOp",EDGE,"E5.bottom")]}),1.0]])],"derivedFrom":subQ0})])],"isStart":false})});}
            fillet(context, id + "F14", {"entities" : qUnion([Q0, Q1, Q2, Q3, Q4, Q5, Q6, Q7]), "radius" : 20 * mm, "tangentPropagation" : true, "allowEdgeOverflow" : false});
        }
        {
            var Q0;
            {var subQ0=sQuery(id+"F12.wireOp",EDGE,"E5.top");var subQ1=sQuery(id+"F0.wireOp",EDGE,"E0.left");var subQ2=makeQuery(id+"F2.opExtrude","CAP_FACE",FACE,{"disambiguationData":[OSD([sQuery(id+"F0.wireOp",EDGE,"E0.bottom"),sQuery(id+"F0.wireOp",EDGE,"E0.top"),subQ1,sQuery(id+"F0.wireOp",EDGE,"E0.right")])],"isStart":false});var subQ4=makeQuery(id+"F12.imprint","INTERSECT",VERTEX,{"derivedFrom":[makeQuery(id+"F11.opFillet","BLEND_EDGE",EDGE,{"blendedFrom":[makeQuery(id+"F2.opExtrude","CAP_EDGE",EDGE,{"disambiguationData":[OSD([subQ1])],"isStart":false}),subQ2],"blendedInto":[subQ2]}),subQ0]});Q0=makeQuery(id+"F13.boolean.opBoolean","INTERSECT",EDGE,{"derivedFrom":[makeQuery(id+"F2.opExtrude","SWEPT_FACE",FACE,{"disambiguationData":[OSD([subQ1])]}),makeQuery(id+"F13.opExtrude","SWEPT_FACE",FACE,{"disambiguationData":[OSD([subQ0]),TDD([makeQuery(id+"F12.imprint","IMPRINT",EDGE,{"disambiguationData":[TD([[makeQuery(id+"F12.imprint","INTERSECT",VERTEX,{"derivedFrom":[subQ0,sQuery(id+"F12.wireOp",EDGE,"E5.left")]}),-1.0]])],"derivedFrom":subQ0}),makeQuery(id+"F12.imprint","IMPRINT",EDGE,{"disambiguationData":[TD([[subQ4,-1.0]])],"derivedFrom":subQ0}),makeQuery(id+"F12.imprint","IMPRINT",EDGE,{"disambiguationData":[TD([[makeQuery(id+"F12.imprint","INTERSECT",VERTEX,{"derivedFrom":[sQuery(id+"F12.wireOp",EDGE,"E4.left"),subQ0]}),1.0]])],"derivedFrom":subQ0})])]})]});}
            var Q1;
            {var subQ0=sQuery(id+"F12.wireOp",EDGE,"E4.left");var subQ1=sQuery(id+"F0.wireOp",EDGE,"E0.bottom");var subQ2=makeQuery(id+"F2.opExtrude","CAP_FACE",FACE,{"disambiguationData":[OSD([subQ1,sQuery(id+"F0.wireOp",EDGE,"E0.top"),sQuery(id+"F0.wireOp",EDGE,"E0.left"),sQuery(id+"F0.wireOp",EDGE,"E0.right")])],"isStart":false});var subQ4=makeQuery(id+"F12.imprint","INTERSECT",VERTEX,{"derivedFrom":[makeQuery(id+"F11.opFillet","BLEND_EDGE",EDGE,{"blendedFrom":[makeQuery(id+"F2.opExtrude","CAP_EDGE",EDGE,{"disambiguationData":[OSD([subQ1])],"isStart":false}),subQ2],"blendedInto":[subQ2]}),subQ0]});Q1=makeQuery(id+"F13.boolean.opBoolean","INTERSECT",EDGE,{"derivedFrom":[makeQuery(id+"F2.opExtrude","SWEPT_FACE",FACE,{"disambiguationData":[OSD([subQ1])]}),makeQuery(id+"F13.opExtrude","SWEPT_FACE",FACE,{"disambiguationData":[OSD([subQ0]),TDD([makeQuery(id+"F12.imprint","IMPRINT",EDGE,{"disambiguationData":[TD([[makeQuery(id+"F12.imprint","INTERSECT",VERTEX,{"derivedFrom":[sQuery(id+"F12.wireOp",EDGE,"E4.bottom"),subQ0]}),-1.0]])],"derivedFrom":subQ0}),makeQuery(id+"F12.imprint","IMPRINT",EDGE,{"disambiguationData":[TD([[subQ4,-1.0]])],"derivedFrom":subQ0}),makeQuery(id+"F12.imprint","IMPRINT",EDGE,{"disambiguationData":[TD([[makeQuery(id+"F12.imprint","INTERSECT",VERTEX,{"derivedFrom":[subQ0,sQuery(id+"F12.wireOp",EDGE,"E5.bottom")]}),1.0]])],"derivedFrom":subQ0})])]})]});}
            var Q2;
            {var subQ0=sQuery(id+"F12.wireOp",EDGE,"E5.bottom");var subQ1=sQuery(id+"F0.wireOp",EDGE,"E0.right");var subQ2=makeQuery(id+"F2.opExtrude","CAP_FACE",FACE,{"disambiguationData":[OSD([sQuery(id+"F0.wireOp",EDGE,"E0.bottom"),sQuery(id+"F0.wireOp",EDGE,"E0.top"),sQuery(id+"F0.wireOp",EDGE,"E0.left"),subQ1])],"isStart":false});var subQ3=makeQuery(id+"F12.imprint","INTERSECT",VERTEX,{"derivedFrom":[makeQuery(id+"F11.opFillet","BLEND_EDGE",EDGE,{"blendedFrom":[makeQuery(id+"F2.opExtrude","CAP_EDGE",EDGE,{"disambiguationData":[OSD([subQ1])],"isStart":false}),subQ2],"blendedInto":[subQ2]}),subQ0]});Q2=makeQuery(id+"F13.boolean.opBoolean","INTERSECT",EDGE,{"derivedFrom":[makeQuery(id+"F2.opExtrude","SWEPT_FACE",FACE,{"disambiguationData":[OSD([subQ1])]}),makeQuery(id+"F13.opExtrude","SWEPT_FACE",FACE,{"disambiguationData":[OSD([subQ0]),TDD([makeQuery(id+"F12.imprint","IMPRINT",EDGE,{"disambiguationData":[TD([[makeQuery(id+"F12.imprint","INTERSECT",VERTEX,{"derivedFrom":[sQuery(id+"F12.wireOp",EDGE,"E4.right"),subQ0]}),-1.0]])],"derivedFrom":subQ0}),makeQuery(id+"F12.imprint","IMPRINT",EDGE,{"disambiguationData":[TD([[subQ3,1.0]])],"derivedFrom":subQ0}),makeQuery(id+"F12.imprint","IMPRINT",EDGE,{"disambiguationData":[TD([[makeQuery(id+"F12.imprint","INTERSECT",VERTEX,{"derivedFrom":[subQ0,sQuery(id+"F12.wireOp",EDGE,"E5.right")]}),1.0]])],"derivedFrom":subQ0})])]})]});}
            var Q3;
            {var subQ0=sQuery(id+"F12.wireOp",EDGE,"E4.right");var subQ1=sQuery(id+"F0.wireOp",EDGE,"E0.top");var subQ2=makeQuery(id+"F2.opExtrude","CAP_FACE",FACE,{"disambiguationData":[OSD([sQuery(id+"F0.wireOp",EDGE,"E0.bottom"),subQ1,sQuery(id+"F0.wireOp",EDGE,"E0.left"),sQuery(id+"F0.wireOp",EDGE,"E0.right")])],"isStart":false});var subQ3=makeQuery(id+"F12.imprint","INTERSECT",VERTEX,{"derivedFrom":[makeQuery(id+"F11.opFillet","BLEND_EDGE",EDGE,{"blendedFrom":[makeQuery(id+"F2.opExtrude","CAP_EDGE",EDGE,{"disambiguationData":[OSD([subQ1])],"isStart":false}),subQ2],"blendedInto":[subQ2]}),subQ0]});Q3=makeQuery(id+"F13.boolean.opBoolean","INTERSECT",EDGE,{"derivedFrom":[makeQuery(id+"F2.opExtrude","SWEPT_FACE",FACE,{"disambiguationData":[OSD([subQ1])]}),makeQuery(id+"F13.opExtrude","SWEPT_FACE",FACE,{"disambiguationData":[OSD([subQ0]),TDD([makeQuery(id+"F12.imprint","IMPRINT",EDGE,{"disambiguationData":[TD([[makeQuery(id+"F12.imprint","INTERSECT",VERTEX,{"derivedFrom":[subQ0,sQuery(id+"F12.wireOp",EDGE,"E5.top")]}),-1.0]])],"derivedFrom":subQ0}),makeQuery(id+"F12.imprint","IMPRINT",EDGE,{"disambiguationData":[TD([[subQ3,1.0]])],"derivedFrom":subQ0}),makeQuery(id+"F12.imprint","IMPRINT",EDGE,{"disambiguationData":[TD([[makeQuery(id+"F12.imprint","INTERSECT",VERTEX,{"derivedFrom":[sQuery(id+"F12.wireOp",EDGE,"E4.top"),subQ0]}),1.0]])],"derivedFrom":subQ0})])]})]});}
            fillet(context, id + "F15", {"entities" : qUnion([Q0, Q1, Q2, Q3]), "radius" : 20 * mm, "tangentPropagation" : true, "allowEdgeOverflow" : false});
        }
    });
